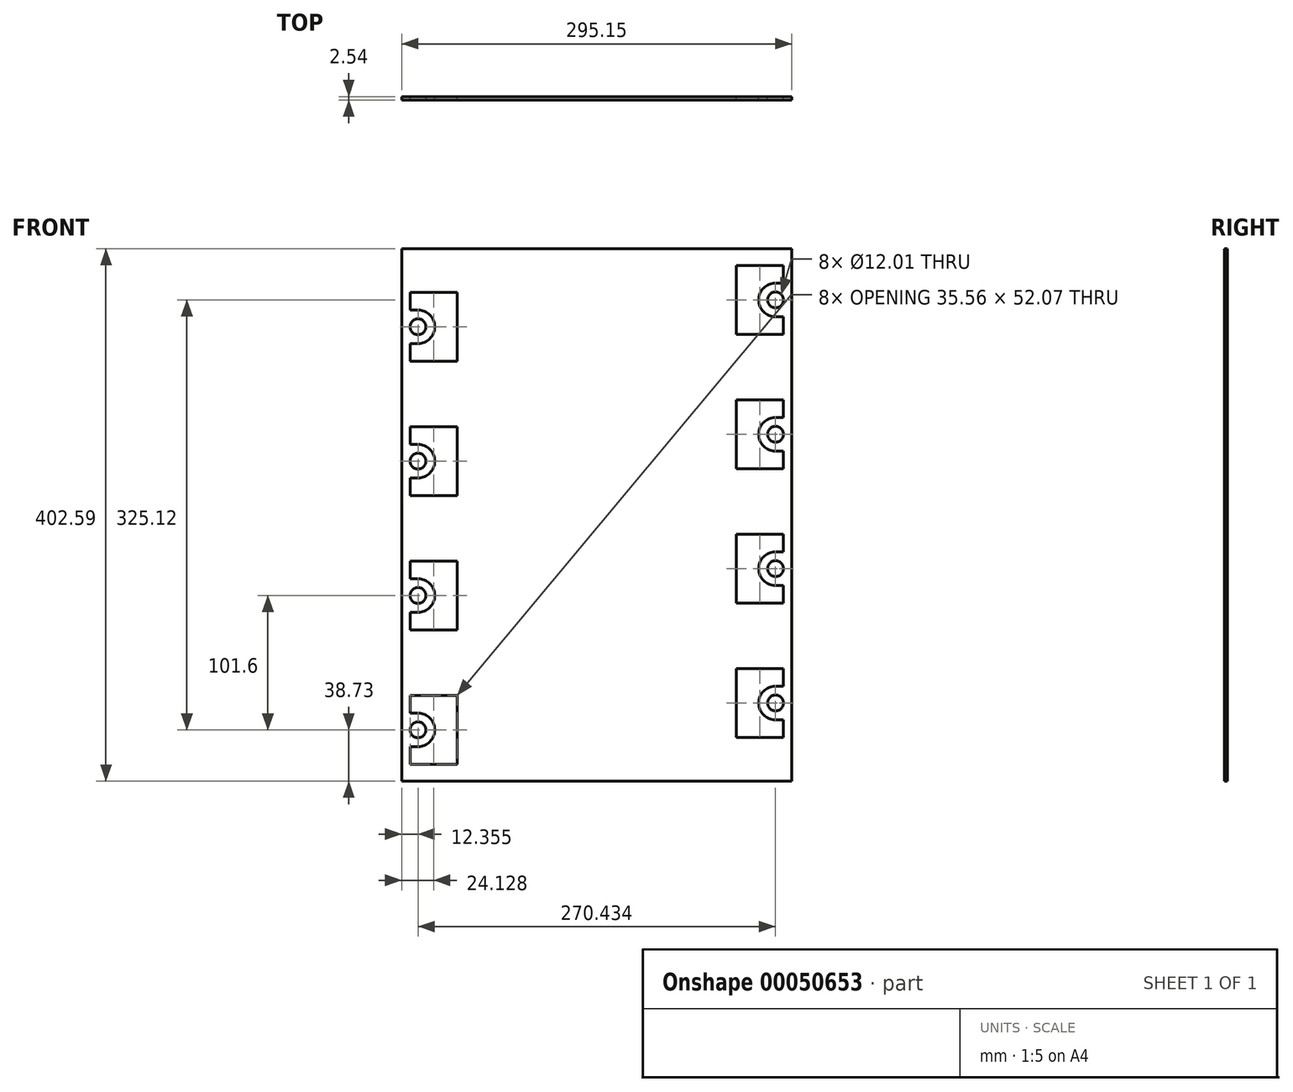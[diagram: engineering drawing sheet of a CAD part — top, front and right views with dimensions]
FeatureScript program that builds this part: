
annotation { "Feature Type Name" : "Feature", "Feature Type Description" : "" }
export const myFeature = defineFeature(function(context is Context, id is Id, definition is map)
    precondition{}
    {
        {
            var Q0;
            Q0=qCreatedBy(makeId("Front.planeOp"),FACE);
            var sketch = newSketch(context, id + "F0", { "sketchPlane" : qUnion([Q0])});
            skLineSegment(sketch, "E0.bottom", {"start": v(-30.66, 46.05) * mm, "end": v(4.9, 46.05) * mm});
            skLineSegment(sketch, "E0.top", {"start": v(-30.66, -6.02) * mm, "end": v(4.9, -6.02) * mm});
            skLineSegment(sketch, "E0.left", {"start": v(-30.66, 46.05) * mm, "end": v(-30.66, 32.71) * mm});
            skLineSegment(sketch, "E0.right", {"start": v(4.9, 46.05) * mm, "end": v(4.9, -6.02) * mm});
            skCircle(sketch, "E1", {"center": v(-24.65, 20.01) * mm, "radius": 6 * mm});
            skPoint(sketch, "E1.centerSnap0", {"position": v(-30.66, 20.01) * mm});
            skArc(sketch, "E2", {"start": v(-24.65, 7.31) * mm, "mid": v(-11.95, 20.01) * mm, "end": v(-24.65, 32.71) * mm});
            skLineSegment(sketch, "E3", {"start": v(-24.65, 32.71) * mm, "end": v(-30.66, 32.71) * mm});
            skLineSegment(sketch, "E4", {"start": v(-24.65, 7.31) * mm, "end": v(-30.66, 7.31) * mm});
            skLineSegment(sketch, "E5.trimOffspring", {"start": v(-30.66, 7.31) * mm, "end": v(-30.66, -6.02) * mm});
            skLineSegment(sketch, "E6", {"start": v(110.56, 111.04) * mm, "end": v(110.56, -247.55) * mm, "construction": true});
            skPoint(sketch, "E7.0.1.0", {"position": v(-30.66, -81.59) * mm});
            skLineSegment(sketch, "E7.0.1.1", {"start": v(4.9, -55.55) * mm, "end": v(4.9, -107.62) * mm});
            skCircle(sketch, "E7.0.1.2", {"center": v(-24.65, -81.59) * mm, "radius": 6 * mm});
            skArc(sketch, "E7.0.1.3", {"start": v(-24.65, -94.29) * mm, "mid": v(-11.95, -81.59) * mm, "end": v(-24.65, -68.89) * mm});
            skLineSegment(sketch, "E7.0.1.4", {"start": v(-30.66, -107.62) * mm, "end": v(4.9, -107.62) * mm});
            skLineSegment(sketch, "E7.0.1.5", {"start": v(-30.66, -55.55) * mm, "end": v(4.9, -55.55) * mm});
            skLineSegment(sketch, "E7.0.1.6", {"start": v(-30.66, -55.55) * mm, "end": v(-30.66, -68.89) * mm});
            skLineSegment(sketch, "E7.0.1.7", {"start": v(-30.66, -94.29) * mm, "end": v(-30.66, -107.62) * mm});
            skLineSegment(sketch, "E7.0.1.8", {"start": v(-24.65, -68.89) * mm, "end": v(-30.66, -68.89) * mm});
            skLineSegment(sketch, "E7.0.1.9", {"start": v(-24.65, -94.29) * mm, "end": v(-30.66, -94.29) * mm});
            skPoint(sketch, "E7.0.2.0", {"position": v(-30.66, -183.19) * mm});
            skLineSegment(sketch, "E7.0.2.1", {"start": v(4.9, -157.15) * mm, "end": v(4.9, -209.22) * mm});
            skCircle(sketch, "E7.0.2.2", {"center": v(-24.65, -183.19) * mm, "radius": 6 * mm});
            skArc(sketch, "E7.0.2.3", {"start": v(-24.65, -195.89) * mm, "mid": v(-11.95, -183.19) * mm, "end": v(-24.65, -170.49) * mm});
            skLineSegment(sketch, "E7.0.2.4", {"start": v(-30.66, -209.22) * mm, "end": v(4.9, -209.22) * mm});
            skLineSegment(sketch, "E7.0.2.5", {"start": v(-30.66, -157.15) * mm, "end": v(4.9, -157.15) * mm});
            skLineSegment(sketch, "E7.0.2.6", {"start": v(-30.66, -157.15) * mm, "end": v(-30.66, -170.49) * mm});
            skLineSegment(sketch, "E7.0.2.7", {"start": v(-30.66, -195.89) * mm, "end": v(-30.66, -209.22) * mm});
            skLineSegment(sketch, "E7.0.2.8", {"start": v(-24.65, -170.49) * mm, "end": v(-30.66, -170.49) * mm});
            skLineSegment(sketch, "E7.0.2.9", {"start": v(-24.65, -195.89) * mm, "end": v(-30.66, -195.89) * mm});
            skPoint(sketch, "E7.0.3.0", {"position": v(-30.66, -284.79) * mm});
            skLineSegment(sketch, "E7.0.3.1", {"start": v(4.9, -258.75) * mm, "end": v(4.9, -310.82) * mm});
            skCircle(sketch, "E7.0.3.2", {"center": v(-24.65, -284.79) * mm, "radius": 6 * mm});
            skArc(sketch, "E7.0.3.3", {"start": v(-24.65, -297.49) * mm, "mid": v(-11.95, -284.79) * mm, "end": v(-24.65, -272.09) * mm});
            skLineSegment(sketch, "E7.0.3.4", {"start": v(-30.66, -310.82) * mm, "end": v(4.9, -310.82) * mm});
            skLineSegment(sketch, "E7.0.3.5", {"start": v(-30.66, -258.75) * mm, "end": v(4.9, -258.75) * mm});
            skLineSegment(sketch, "E7.0.3.6", {"start": v(-30.66, -258.75) * mm, "end": v(-30.66, -272.09) * mm});
            skLineSegment(sketch, "E7.0.3.7", {"start": v(-30.66, -297.49) * mm, "end": v(-30.66, -310.82) * mm});
            skLineSegment(sketch, "E7.0.3.8", {"start": v(-24.65, -272.09) * mm, "end": v(-30.66, -272.09) * mm});
            skLineSegment(sketch, "E7.0.3.9", {"start": v(-24.65, -297.49) * mm, "end": v(-30.66, -297.49) * mm});
            skLineSegment(sketch, "E7.direction1", {"start": v(-30.66, -6.02) * mm, "end": v(5, -6.02) * mm, "construction": true});
            skLineSegment(sketch, "E7.direction2", {"start": v(-30.66, -6.02) * mm, "end": v(-30.66, -107.62) * mm, "construction": true});
            skLineSegment(sketch, "E8", {"start": v(4.9, -107.62) * mm, "end": v(4.9, -157.15) * mm, "construction": true});
            skPoint(sketch, "E9", {"position": v(4.9, -132.39) * mm});
            skLineSegment(sketch, "E10", {"start": v(4.9, -132.39) * mm, "end": v(110.56, -132.39) * mm, "construction": true});
            skPoint(sketch, "E11", {"position": v(110.56, -122.23) * mm});
            skLineSegment(sketch, "E12.1.0", {"start": v(251.79, 14.3) * mm, "end": v(216.23, 14.3) * mm});
            skPoint(sketch, "E12.1.1", {"position": v(216.23, -112.07) * mm});
            skLineSegment(sketch, "E12.1.2", {"start": v(251.79, -35.23) * mm, "end": v(216.23, -35.23) * mm});
            skLineSegment(sketch, "E12.1.3", {"start": v(251.79, 66.37) * mm, "end": v(216.23, 66.37) * mm});
            skPoint(sketch, "E12.1.4", {"position": v(251.79, -61.27) * mm});
            skLineSegment(sketch, "E12.1.5", {"start": v(251.79, -87.3) * mm, "end": v(216.23, -87.3) * mm});
            skArc(sketch, "E12.1.6", {"start": v(245.78, 53.03) * mm, "mid": v(233.08, 40.33) * mm, "end": v(245.78, 27.63) * mm});
            skArc(sketch, "E12.1.7", {"start": v(245.78, -48.57) * mm, "mid": v(233.08, -61.27) * mm, "end": v(245.78, -73.97) * mm});
            skPoint(sketch, "E12.1.8", {"position": v(251.79, 40.33) * mm});
            skLineSegment(sketch, "E12.1.9", {"start": v(216.23, 14.3) * mm, "end": v(216.23, 66.37) * mm});
            skLineSegment(sketch, "E12.1.10", {"start": v(216.23, -87.3) * mm, "end": v(216.23, -35.23) * mm});
            skCircle(sketch, "E12.1.11", {"center": v(245.78, 40.33) * mm, "radius": 6 * mm});
            skLineSegment(sketch, "E12.1.12", {"start": v(251.79, -48.57) * mm, "end": v(251.79, -35.23) * mm});
            skLineSegment(sketch, "E12.1.13", {"start": v(251.79, 53.03) * mm, "end": v(251.79, 66.37) * mm});
            skCircle(sketch, "E12.1.14", {"center": v(245.78, -61.27) * mm, "radius": 6 * mm});
            skLineSegment(sketch, "E12.1.15", {"start": v(251.79, 14.3) * mm, "end": v(251.79, 27.63) * mm});
            skLineSegment(sketch, "E12.1.16", {"start": v(251.79, -87.3) * mm, "end": v(251.79, -73.97) * mm});
            skLineSegment(sketch, "E12.1.17", {"start": v(245.78, -73.97) * mm, "end": v(251.79, -73.97) * mm});
            skLineSegment(sketch, "E12.1.18", {"start": v(245.78, 27.63) * mm, "end": v(251.79, 27.63) * mm});
            skLineSegment(sketch, "E12.1.19", {"start": v(245.78, 53.03) * mm, "end": v(251.79, 53.03) * mm});
            skLineSegment(sketch, "E12.1.20", {"start": v(216.23, -136.83) * mm, "end": v(216.23, -87.3) * mm, "construction": true});
            skLineSegment(sketch, "E12.1.21", {"start": v(245.78, -48.57) * mm, "end": v(251.79, -48.57) * mm});
            skLineSegment(sketch, "E12.1.22", {"start": v(251.79, -238.43) * mm, "end": v(251.79, -136.83) * mm, "construction": true});
            skPoint(sketch, "E12.1.23", {"position": v(251.79, -264.47) * mm});
            skLineSegment(sketch, "E12.1.24", {"start": v(251.79, -238.43) * mm, "end": v(216.13, -238.43) * mm, "construction": true});
            skArc(sketch, "E12.1.25", {"start": v(245.78, -150.17) * mm, "mid": v(233.08, -162.87) * mm, "end": v(245.78, -175.57) * mm});
            skLineSegment(sketch, "E12.1.26", {"start": v(216.23, -188.9) * mm, "end": v(216.23, -136.83) * mm});
            skLineSegment(sketch, "E12.1.27", {"start": v(251.79, -136.83) * mm, "end": v(216.23, -136.83) * mm});
            skLineSegment(sketch, "E12.1.28", {"start": v(251.79, -188.9) * mm, "end": v(216.23, -188.9) * mm});
            skPoint(sketch, "E12.1.29", {"position": v(251.79, -162.87) * mm});
            skLineSegment(sketch, "E12.1.30", {"start": v(216.23, -290.5) * mm, "end": v(216.23, -238.43) * mm});
            skArc(sketch, "E12.1.31", {"start": v(245.78, -251.77) * mm, "mid": v(233.08, -264.47) * mm, "end": v(245.78, -277.17) * mm});
            skLineSegment(sketch, "E12.1.32", {"start": v(251.79, -290.5) * mm, "end": v(216.23, -290.5) * mm});
            skLineSegment(sketch, "E12.1.33", {"start": v(251.79, -238.43) * mm, "end": v(216.23, -238.43) * mm});
            skLineSegment(sketch, "E12.1.34", {"start": v(245.78, -175.57) * mm, "end": v(251.79, -175.57) * mm});
            skCircle(sketch, "E12.1.35", {"center": v(245.78, -162.87) * mm, "radius": 6 * mm});
            skLineSegment(sketch, "E12.1.36", {"start": v(251.79, -188.9) * mm, "end": v(251.79, -175.57) * mm});
            skLineSegment(sketch, "E12.1.37", {"start": v(251.79, -290.5) * mm, "end": v(251.79, -277.17) * mm});
            skCircle(sketch, "E12.1.38", {"center": v(245.78, -264.47) * mm, "radius": 6 * mm});
            skLineSegment(sketch, "E12.1.39", {"start": v(251.79, -150.17) * mm, "end": v(251.79, -136.83) * mm});
            skLineSegment(sketch, "E12.1.40", {"start": v(245.78, -150.17) * mm, "end": v(251.79, -150.17) * mm});
            skLineSegment(sketch, "E12.1.41", {"start": v(251.79, -251.77) * mm, "end": v(251.79, -238.43) * mm});
            skLineSegment(sketch, "E12.1.42", {"start": v(245.78, -277.17) * mm, "end": v(251.79, -277.17) * mm});
            skLineSegment(sketch, "E12.1.43", {"start": v(245.78, -251.77) * mm, "end": v(251.79, -251.77) * mm});
            skLineSegment(sketch, "E13.bottom", {"start": v(258.14, 79.07) * mm, "end": v(-37.01, 79.07) * mm});
            skLineSegment(sketch, "E13.top", {"start": v(258.14, -323.52) * mm, "end": v(-37.01, -323.52) * mm});
            skLineSegment(sketch, "E13.left", {"start": v(258.14, 79.07) * mm, "end": v(258.14, -323.52) * mm});
            skLineSegment(sketch, "E13.right", {"start": v(-37.01, 79.07) * mm, "end": v(-37.01, -323.52) * mm});
            skSolve(sketch);
        }
        {
            var Q0;
            Q0=makeQuery(id+"F0.imprint","IMPRINT",FACE,{"disambiguationData":[TD([[makeQuery(id+"F0.imprint","IMPRINT",EDGE,{"derivedFrom":sQuery(id+"F0.wireOp",EDGE,"E0.bottom")}),1.0]])]});
            extrude(context, id + "F1", {"entities" : qUnion([Q0]), "depth" : 2.54 * mm});
        }
    });
